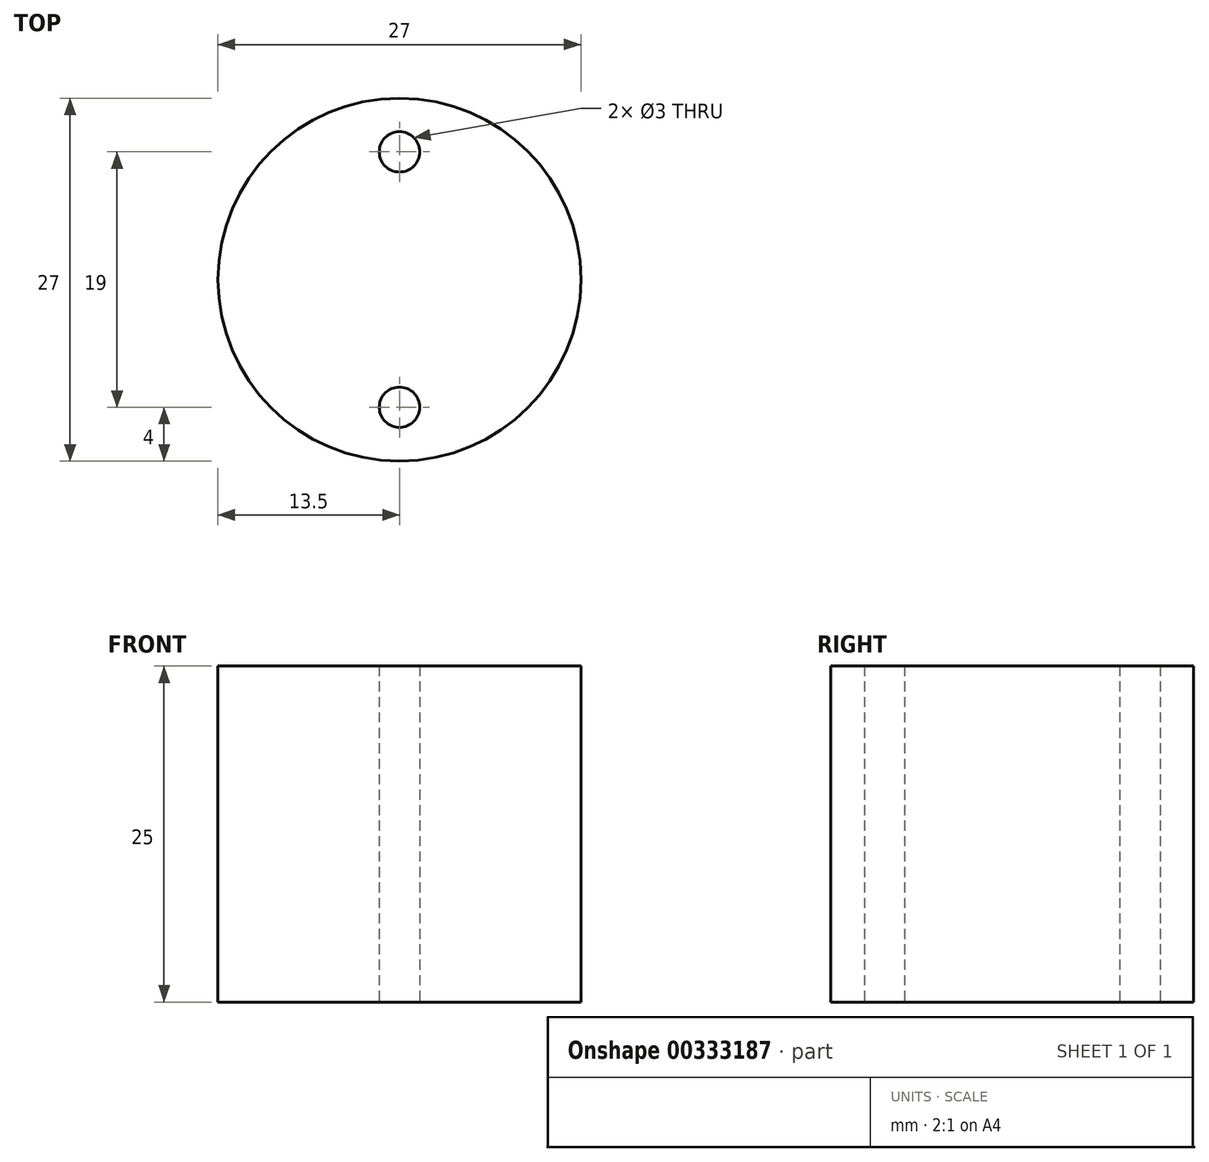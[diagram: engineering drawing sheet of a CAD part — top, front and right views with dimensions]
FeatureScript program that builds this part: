
annotation { "Feature Type Name" : "Feature", "Feature Type Description" : "" }
export const myFeature = defineFeature(function(context is Context, id is Id, definition is map)
    precondition{}
    {
        {
            var Q0;
            Q0=qCreatedBy(makeId("Top.planeOp"),FACE);
            var sketch = newSketch(context, id + "F0", { "sketchPlane" : qUnion([Q0])});
            skCircle(sketch, "E0", {"center": v(0, 0) * mm, "radius": 13.5 * mm});
            skCircle(sketch, "E1", {"center": v(0, 9.5) * mm, "radius": 1.5 * mm});
            skCircle(sketch, "E2", {"center": v(0, -9.5) * mm, "radius": 1.5 * mm});
            skSolve(sketch);
        }
        {
            var Q0;
            Q0=qSketchRegion(id+"F0",true);
            extrude(context, id + "F1", {"entities" : qUnion([Q0]), "depth" : 25 * mm});
        }
    });
